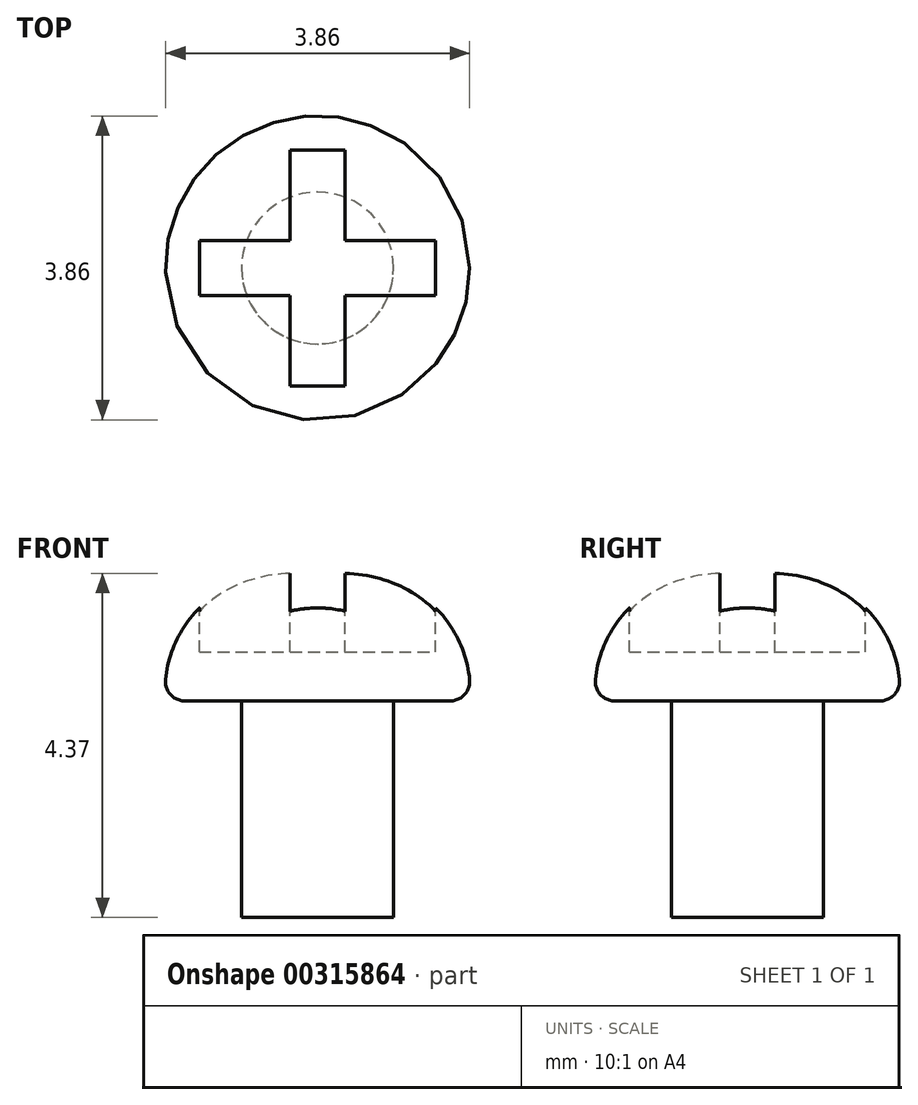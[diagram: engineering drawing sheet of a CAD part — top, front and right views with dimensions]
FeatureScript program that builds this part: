
annotation { "Feature Type Name" : "Feature", "Feature Type Description" : "" }
export const myFeature = defineFeature(function(context is Context, id is Id, definition is map)
    precondition{}
    {
        {
            var Q0;
            Q0=qCreatedBy(makeId("Top.planeOp"),FACE);
            var sketch = newSketch(context, id + "F0", { "sketchPlane" : qUnion([Q0])});
            skCircle(sketch, "E0", {"center": v(0, 0) * mm, "radius": 1.94 * mm});
            skSolve(sketch);
        }
        {
            var Q0;
            Q0 = qSketchRegion(id + "F0", true);
            extrude(context, id + "F1", {"entities" : qUnion([Q0]), "depth" : 1.62 * mm});
        }
        {
            var Q0;
            Q0=makeQuery(id+"F1.opExtrude","CAP_FACE",FACE,{"disambiguationData":[OSD([sQuery(id+"F0.wireOp",EDGE,"E0")])],"isStart":false});
            var sketch = newSketch(context, id + "F2", { "sketchPlane" : qUnion([Q0])});
            skLineSegment(sketch, "E1.bottom", {"start": v(-0.35, -1.5) * mm, "end": v(0.35, -1.5) * mm});
            skLineSegment(sketch, "E1.top", {"start": v(-0.35, 1.5) * mm, "end": v(0.35, 1.5) * mm});
            skLineSegment(sketch, "E1.left", {"start": v(-0.35, -1.5) * mm, "end": v(-0.35, 1.5) * mm});
            skLineSegment(sketch, "E1.right", {"start": v(0.35, -1.5) * mm, "end": v(0.35, 1.5) * mm});
            skLineSegment(sketch, "E2.bottom", {"start": v(-1.5, -0.35) * mm, "end": v(1.5, -0.35) * mm});
            skLineSegment(sketch, "E2.top", {"start": v(-1.5, 0.35) * mm, "end": v(1.5, 0.35) * mm});
            skLineSegment(sketch, "E2.left", {"start": v(-1.5, -0.35) * mm, "end": v(-1.5, 0.35) * mm});
            skLineSegment(sketch, "E2.right", {"start": v(1.5, -0.35) * mm, "end": v(1.5, 0.35) * mm});
            skSolve(sketch);
        }
        {
            var Q0;
            Q0 = qSketchRegion(id + "F2", true);
            extrude(context, id + "F3", {"entities" : qUnion([Q0]), "operationType" : NewBodyOperationType.REMOVE, "oppositeDirection" : true, "depth" : 1 * mm});
        }
        {
            var Q0;
            Q0=makeQuery(id+"F1.opExtrude","CAP_EDGE",EDGE,{"disambiguationData":[OSD([sQuery(id+"F0.wireOp",EDGE,"E0")])],"isStart":false});
            fillet(context, id + "F4", {"entities" : qUnion([Q0]), "radius" : 1.5 * mm, "tangentPropagation" : true, "allowEdgeOverflow" : false});
        }
        {
            var Q0;
            Q0=makeQuery(id+"F1.opExtrude","CAP_EDGE",EDGE,{"disambiguationData":[OSD([sQuery(id+"F0.wireOp",EDGE,"E0")])],"isStart":true});
            fillet(context, id + "F5", {"entities" : qUnion([Q0]), "radius" : .25 * mm, "tangentPropagation" : true, "allowEdgeOverflow" : false});
        }
        {
            var Q0;
            Q0=makeQuery(id+"F1.opExtrude","CAP_FACE",FACE,{"disambiguationData":[OSD([sQuery(id+"F0.wireOp",EDGE,"E0")])],"isStart":true});
            var sketch = newSketch(context, id + "F6", { "sketchPlane" : qUnion([Q0])});
            skCircle(sketch, "E3", {"center": v(0, 0) * mm, "radius": 0.97 * mm});
            skSolve(sketch);
        }
        {
            var Q0;
            Q0=makeQuery(id+"F6.imprint","IMPRINT",FACE,{"disambiguationData":[TD([[makeQuery(id+"F6.imprint","IMPRINT",EDGE,{"derivedFrom":sQuery(id+"F6.wireOp",EDGE,"E3")}),1.0]])]});
            extrude(context, id + "F7", {"entities" : qUnion([Q0]), "operationType" : NewBodyOperationType.ADD, "depth" : 2.75 * mm});
        }
    });
